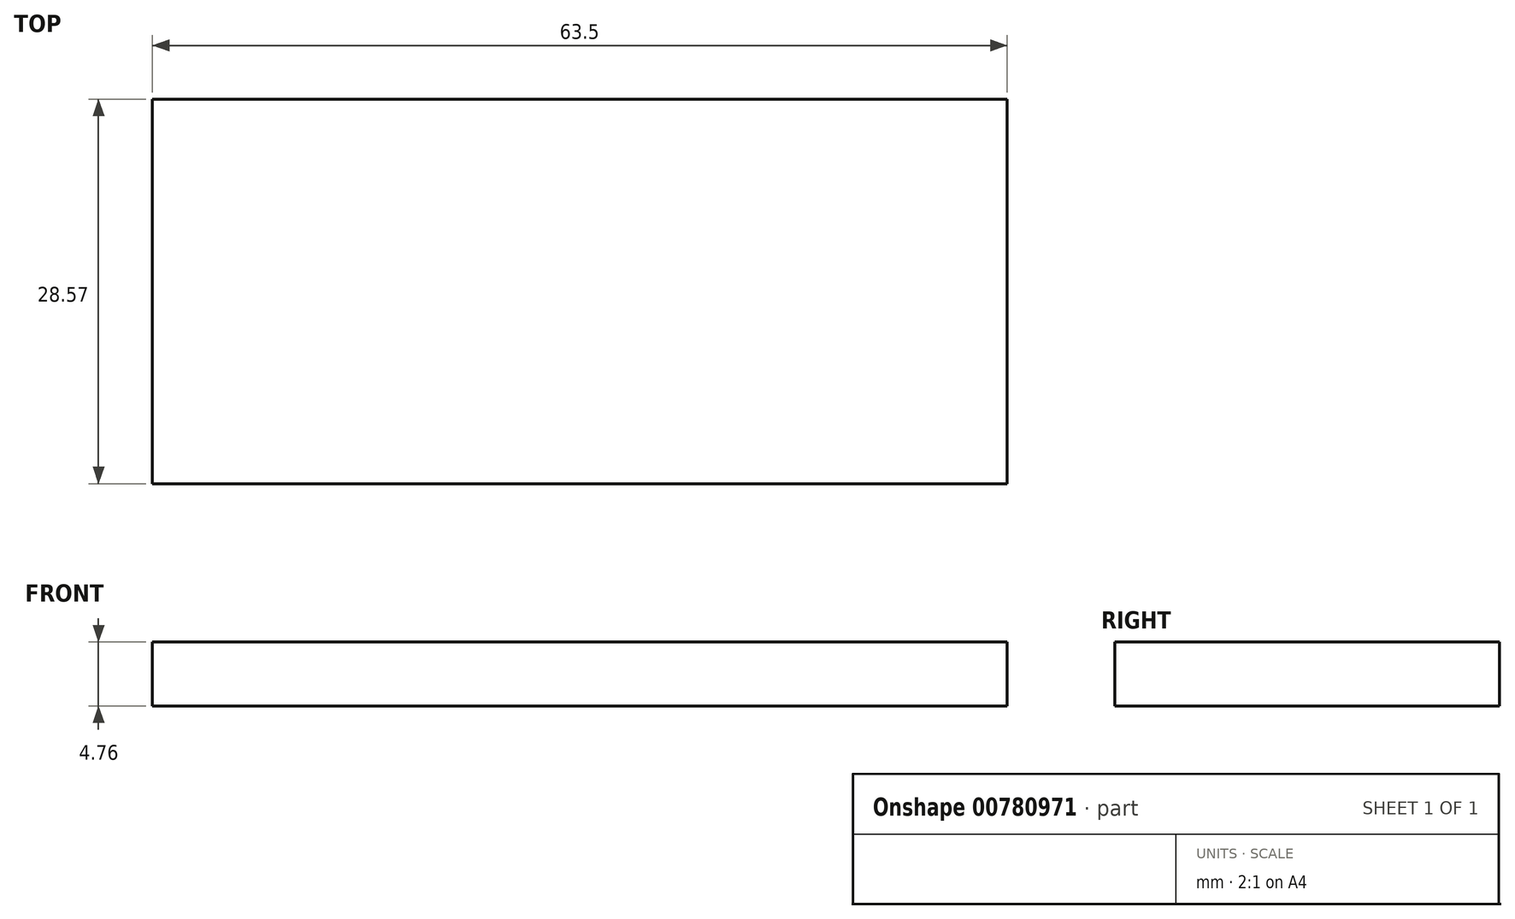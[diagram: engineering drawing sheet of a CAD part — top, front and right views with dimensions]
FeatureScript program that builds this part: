
annotation { "Feature Type Name" : "Feature", "Feature Type Description" : "" }
export const myFeature = defineFeature(function(context is Context, id is Id, definition is map)
    precondition{}
    {
        {
            var Q0;
            Q0=qCreatedBy(makeId("Top.planeOp"),FACE);
            var sketch = newSketch(context, id + "F0", { "sketchPlane" : qUnion([Q0])});
            skLineSegment(sketch, "E0", {"start": v(-63.5, -16.96) * mm, "end": v(0, -16.96) * mm});
            skLineSegment(sketch, "E1", {"start": v(0, -16.96) * mm, "end": v(0, 11.61) * mm});
            skLineSegment(sketch, "E2", {"start": v(0, 11.61) * mm, "end": v(-63.5, 11.61) * mm});
            skLineSegment(sketch, "E3", {"start": v(-63.5, 11.61) * mm, "end": v(-63.5, -16.96) * mm});
            skSolve(sketch);
        }
        {
            var Q0;
            Q0 = qSketchRegion(id + "F0", true);
            extrude(context, id + "F1", {"entities" : qUnion([Q0]), "depth" : 4.76 * mm, "offsetDistance" : 25.4 * mm});
        }
    });
